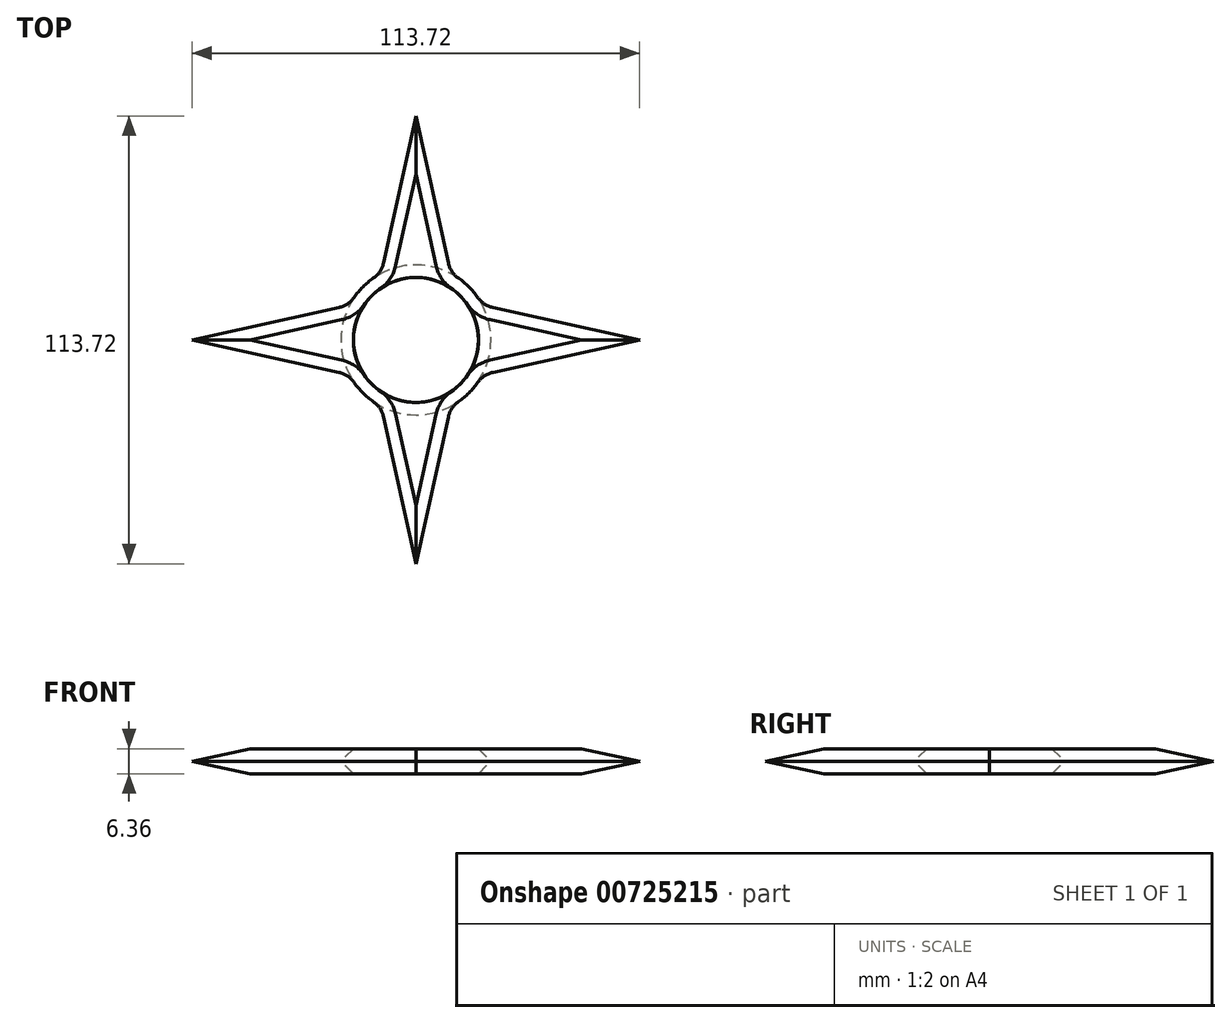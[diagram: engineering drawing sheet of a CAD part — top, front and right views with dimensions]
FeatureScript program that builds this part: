
annotation { "Feature Type Name" : "Feature", "Feature Type Description" : "" }
export const myFeature = defineFeature(function(context is Context, id is Id, definition is map)
    precondition{}
    {
        {
            var Q0;
            Q0=qCreatedBy(makeId("Top.planeOp"),FACE);
            var sketch = newSketch(context, id + "F0", { "sketchPlane" : qUnion([Q0])});
            skArc(sketch, "E0", {"start": v(-10.83, 15.67) * mm, "mid": v(0, -19.05) * mm, "end": v(10.83, 15.67) * mm});
            skLineSegment(sketch, "E1.left", {"start": v(-8.34, 19.05) * mm, "end": v(-8.34, 18.13) * mm});
            skLineSegment(sketch, "E1.right", {"start": v(8.34, 19.05) * mm, "end": v(8.34, 18.13) * mm});
            skPoint(sketch, "E1.middle", {"position": v(0, 19.05) * mm});
            skLineSegment(sketch, "E2", {"start": v(0, 56.86) * mm, "end": v(-8.23, 19.53) * mm});
            skLineSegment(sketch, "E3", {"start": v(0, 56.86) * mm, "end": v(8.23, 19.53) * mm});
            skPoint(sketch, "E1.top.end.orphan", {"position": v(8.34, -18.76) * mm});
            skPoint(sketch, "E4.orphan", {"position": v(-8.34, -18.76) * mm});
            skPoint(sketch, "E1.bottom.end.orphan", {"position": v(8.34, 56.86) * mm});
            skPoint(sketch, "E5.orphan", {"position": v(-8.34, 56.86) * mm});
            skPoint(sketch, "E6.newPointB", {"position": v(-8.34, 19.05) * mm});
            skArc(sketch, "E6.filletArc", {"start": v(-10.83, 15.67) * mm, "mid": v(-9.16, 17.36) * mm, "end": v(-8.23, 19.53) * mm});
            skPoint(sketch, "E7.newPointA", {"position": v(8.34, 19.05) * mm});
            skArc(sketch, "E7.filletArc", {"start": v(8.23, 19.53) * mm, "mid": v(9.16, 17.36) * mm, "end": v(10.83, 15.67) * mm});
            skSolve(sketch);
        }
        {
            var Q0;
            Q0 = qSketchRegion(id + "F0", true);
            extrude(context, id + "F1", {"entities" : qUnion([Q0]), "endBound" : BoundingType.SYMMETRIC, "depth" : 6.35 * mm, "offsetDistance" : 25.4 * mm});
        }
        {
            var Q0;
            Q0=makeQuery(id+"F1.opExtrude","SWEPT_BODY",BODY,{"disambiguationData":[OSD([sQuery(id+"F0.wireOp",EDGE,"E0"),sQuery(id+"F0.wireOp",EDGE,"E2"),sQuery(id+"F0.wireOp",EDGE,"E3"),sQuery(id+"F0.wireOp",EDGE,"E6.filletArc"),sQuery(id+"F0.wireOp",EDGE,"E7.filletArc")])]});
            var Q1;
            Q1=makeQuery(id+"F1.opExtrude","SWEPT_FACE",FACE,{"disambiguationData":[OSD([sQuery(id+"F0.wireOp",EDGE,"E0")])]});
            circularPattern(context, id + "F2", {"entities" : qUnion([Q0]), "axis" : qUnion([Q1]), "angle" : 360 * degree, "instanceCount" : 4, "equalSpace" : true});
        }
        {
            var Q0;
            Q0=makeQuery(id+"F2.opPattern","COPY",FACE,{"derivedFrom":makeQuery(id+"F1.opExtrude","CAP_FACE",FACE,{"disambiguationData":[OSD([sQuery(id+"F0.wireOp",EDGE,"E0"),sQuery(id+"F0.wireOp",EDGE,"E2"),sQuery(id+"F0.wireOp",EDGE,"E3"),sQuery(id+"F0.wireOp",EDGE,"E6.filletArc"),sQuery(id+"F0.wireOp",EDGE,"E7.filletArc")])],"isStart":false}),"instanceName":"1"});
            var Q1;
            Q1=makeQuery(id+"F1.opExtrude","CAP_FACE",FACE,{"disambiguationData":[OSD([sQuery(id+"F0.wireOp",EDGE,"E0"),sQuery(id+"F0.wireOp",EDGE,"E2"),sQuery(id+"F0.wireOp",EDGE,"E3"),sQuery(id+"F0.wireOp",EDGE,"E6.filletArc"),sQuery(id+"F0.wireOp",EDGE,"E7.filletArc")])],"isStart":false});
            var Q2;
            Q2=makeQuery(id+"F2.opPattern","COPY",FACE,{"derivedFrom":makeQuery(id+"F1.opExtrude","CAP_FACE",FACE,{"disambiguationData":[OSD([sQuery(id+"F0.wireOp",EDGE,"E0"),sQuery(id+"F0.wireOp",EDGE,"E2"),sQuery(id+"F0.wireOp",EDGE,"E3"),sQuery(id+"F0.wireOp",EDGE,"E6.filletArc"),sQuery(id+"F0.wireOp",EDGE,"E7.filletArc")])],"isStart":false}),"instanceName":"3"});
            var Q3;
            Q3=makeQuery(id+"F2.opPattern","COPY",FACE,{"derivedFrom":makeQuery(id+"F1.opExtrude","CAP_FACE",FACE,{"disambiguationData":[OSD([sQuery(id+"F0.wireOp",EDGE,"E0"),sQuery(id+"F0.wireOp",EDGE,"E2"),sQuery(id+"F0.wireOp",EDGE,"E3"),sQuery(id+"F0.wireOp",EDGE,"E6.filletArc"),sQuery(id+"F0.wireOp",EDGE,"E7.filletArc")])],"isStart":false}),"instanceName":"2"});
            var Q4;
            Q4=makeQuery(id+"F2.opPattern","COPY",FACE,{"derivedFrom":makeQuery(id+"F1.opExtrude","CAP_FACE",FACE,{"disambiguationData":[OSD([sQuery(id+"F0.wireOp",EDGE,"E0"),sQuery(id+"F0.wireOp",EDGE,"E2"),sQuery(id+"F0.wireOp",EDGE,"E3"),sQuery(id+"F0.wireOp",EDGE,"E6.filletArc"),sQuery(id+"F0.wireOp",EDGE,"E7.filletArc")])],"isStart":true}),"instanceName":"1"});
            var Q5;
            Q5=makeQuery(id+"F2.opPattern","COPY",FACE,{"derivedFrom":makeQuery(id+"F1.opExtrude","CAP_FACE",FACE,{"disambiguationData":[OSD([sQuery(id+"F0.wireOp",EDGE,"E0"),sQuery(id+"F0.wireOp",EDGE,"E2"),sQuery(id+"F0.wireOp",EDGE,"E3"),sQuery(id+"F0.wireOp",EDGE,"E6.filletArc"),sQuery(id+"F0.wireOp",EDGE,"E7.filletArc")])],"isStart":true}),"instanceName":"2"});
            var Q6;
            Q6=makeQuery(id+"F2.opPattern","COPY",FACE,{"derivedFrom":makeQuery(id+"F1.opExtrude","CAP_FACE",FACE,{"disambiguationData":[OSD([sQuery(id+"F0.wireOp",EDGE,"E0"),sQuery(id+"F0.wireOp",EDGE,"E2"),sQuery(id+"F0.wireOp",EDGE,"E3"),sQuery(id+"F0.wireOp",EDGE,"E6.filletArc"),sQuery(id+"F0.wireOp",EDGE,"E7.filletArc")])],"isStart":true}),"instanceName":"3"});
            var Q7;
            Q7=makeQuery(id+"F1.opExtrude","CAP_FACE",FACE,{"disambiguationData":[OSD([sQuery(id+"F0.wireOp",EDGE,"E0"),sQuery(id+"F0.wireOp",EDGE,"E2"),sQuery(id+"F0.wireOp",EDGE,"E3"),sQuery(id+"F0.wireOp",EDGE,"E6.filletArc"),sQuery(id+"F0.wireOp",EDGE,"E7.filletArc")])],"isStart":true});
            chamfer(context, id + "F3", {"entities" : qUnion([Q0, Q1, Q2, Q3, Q4, Q5, Q6, Q7]), "width" : 3.17 * mm, "tangentPropagation" : true});
        }
    });
